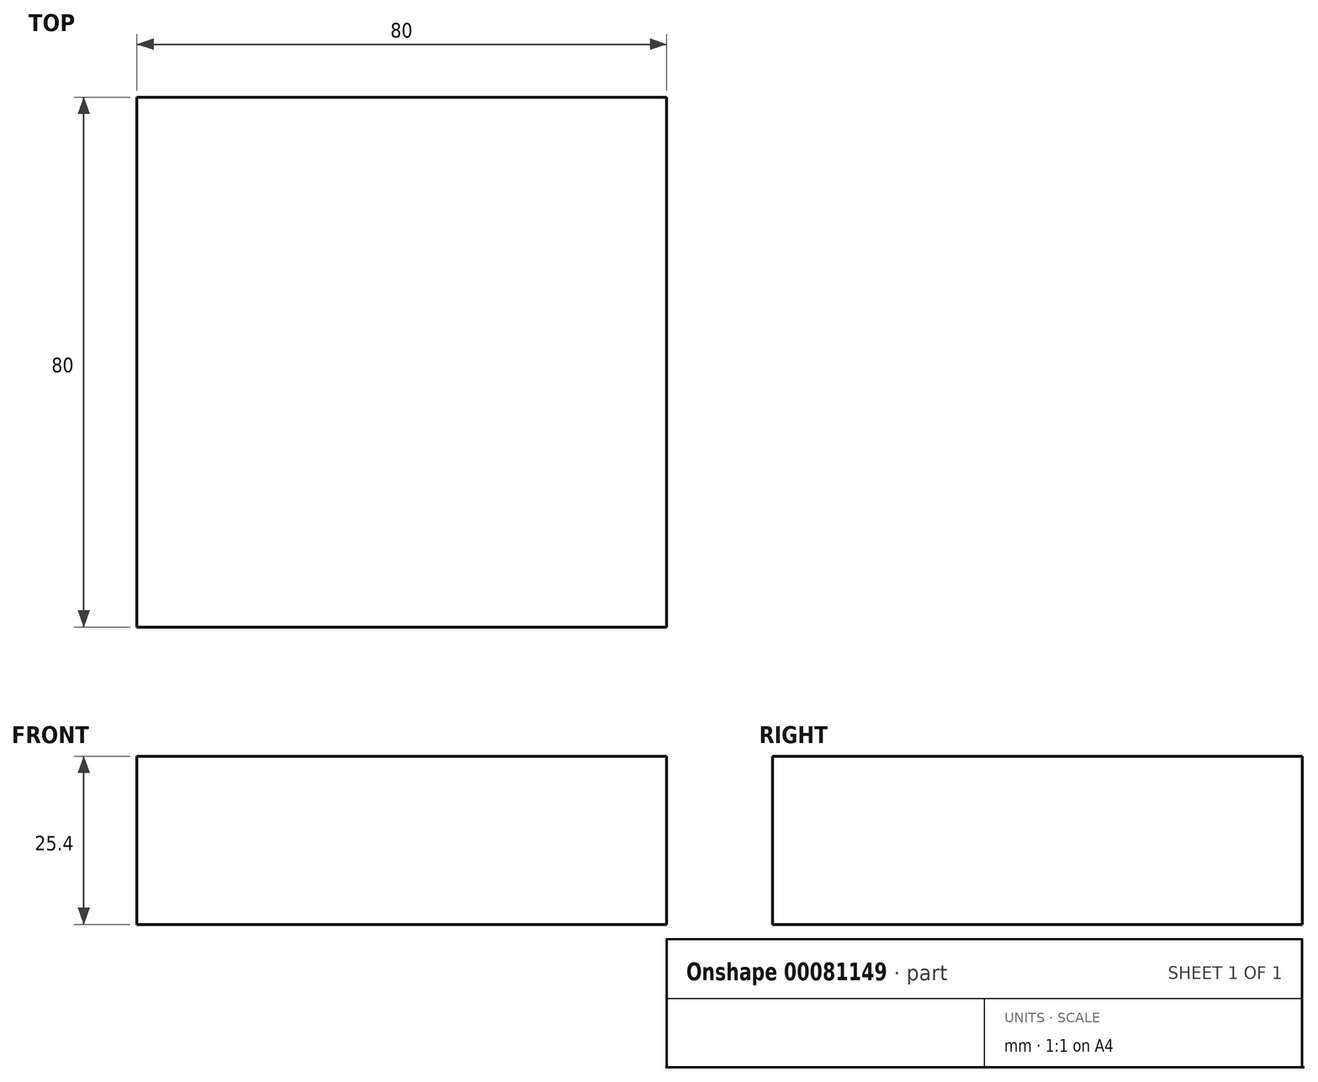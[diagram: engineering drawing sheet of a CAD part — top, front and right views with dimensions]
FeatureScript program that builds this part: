
annotation { "Feature Type Name" : "Feature", "Feature Type Description" : "" }
export const myFeature = defineFeature(function(context is Context, id is Id, definition is map)
    precondition{}
    {
        {
            var Q0;
            Q0=qCreatedBy(makeId("Top.planeOp"),FACE);
            var sketch = newSketch(context, id + "F0", { "sketchPlane" : qUnion([Q0])});
            skLineSegment(sketch, "E0.bottom", {"start": v(0, 0) * mm, "end": v(80, 0) * mm});
            skLineSegment(sketch, "E0.top", {"start": v(0, 80) * mm, "end": v(80, 80) * mm});
            skLineSegment(sketch, "E0.left", {"start": v(0, 0) * mm, "end": v(0, 80) * mm});
            skLineSegment(sketch, "E0.right", {"start": v(80, 0) * mm, "end": v(80, 80) * mm});
            skSolve(sketch);
        }
        {
            var Q0;
            Q0=makeQuery(id+"F0.imprint","IMPRINT",FACE,{"disambiguationData":[TD([[makeQuery(id+"F0.imprint","IMPRINT",EDGE,{"derivedFrom":sQuery(id+"F0.wireOp",EDGE,"E0.bottom")}),1.0]])]});
            extrude(context, id + "F1", {"entities" : qUnion([Q0]), "depth" : 25.4 * mm});
        }
    });
